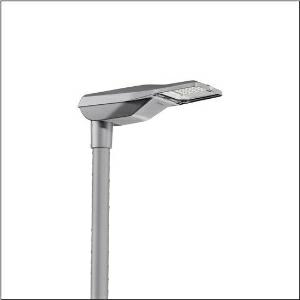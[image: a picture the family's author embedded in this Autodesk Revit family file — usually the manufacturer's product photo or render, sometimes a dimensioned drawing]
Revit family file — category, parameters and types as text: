
# Revit family: streetlight_sl_21_iq_micro___p0_5a_5xe1v31d08db_e47d
name_source: partatom
category: Lighting Fixtures
units: mm (PartAtom-declared; Revit-internal decimal feet)

## family parameters
Cut with Voids When Loaded = No
Host = Face
Light Source = No
Part Type = Normal
Room Calculation Point = No
Round Connector Dimension = Use Diameter
Shared = No

## types (1)
- --- (1 x LED, 4660 lm, 36.4 W, 3000K)
    Apparent Load = 36 VA
    CIE Flux Codes = 37 73 96 100 100
    Color Rendering = 70
    Color Temperature = 3000K
    Default Elevation = 1800 mm
    Description = Streetlight SL 21 iQ micro, mast luminaire, primary light control with lens, of PMMA, primary optical cover: cover, of toughened safety glass, transparent, light distribution: P0.5a, light emission: direct distribution, primary light characteristic: asymmetric, installation type: post-top, side-entry, LED, High Power LED, rated luminous flux: 4.660lm, luminous efficacy: 128lm/W, light colour: 730, colour temperature: 3000K, control gear: iQ-Comfort, control: pre-setting: linear dimming characteristic, Auto-Match, Temp-Guard, Lumen-Switch, Night-Set, Smart-Wire, Light-Fading, Desk-Remote (wireless, voltage-free reading and setting of iQ features in the workshop via application-optimized NFC function/RFID function), optimised constant luminous flux control (CLO 2.0), mains connection: 220..240V, AC, 50/60Hz, start of lifetime: 36W, end of service life: 38W, reduction: 16W, luminaire housing, of diecast aluminium, powder-coated, SITECO metallic grey (DB 702S), corrosivity category C5 high according to DIN EN ISO 12944, please order mast flange separately, inclination adjustable: 0°, 5°, 10°, 15°, sealing non-destructively replaceable, multi-level sealing system, length: 528mm, width: 235mm, height: 110mm, mast flange for spigot size: 42mm (side-entry): 5XC10008XM4, 60/48mm (side-entry/post-top): 5XC10108XM2, 76/60mm (side-entry/post-top): 5XC10108XM1, protection rating (complete): IP66, insulation class (complete): insulation class II (safety insulation), certification: CE, ENEC, ENEC+, VDE, impact resistance: IK10, permissible operating ambient temperature for outdoor applications: -40..+50°C, standard-compliant lighting for roads and squares, packaging unit: 1 piece

Light Distribution: P0.5a
    Height = 110 mm
    Lamp = 1 x LED
    Lamp Light Flux = 4660 lm
    Lamp Power = 36.4 W
    Lamp count = 1
    Length = 528 mm
    Luminous efficacy = 128 lm/W
    Manufacturer = Siteco
    ModVariant = No
    Model = 5XE1V31D08DB
    Number of Poles = 1
    OnlyDefault = Yes
    Power Factor = 1
    Product Name = Streetlight SL 21 iQ micro | P0.5a
    Product group = mast luminaire | pylon top
    ProductGroupID = 6100
    Protection Class = Protection class II
    Protection Degree = IP 66
    RLX_Detail_Level = 1
    RLX_Emergency_Light_Flux = 0 lm
    RLX_Emergency_Type = 0
    RLX_Emergency_Type_DB = No
    RlxData = <blob elided: 99325 chars, md5=adc8d52f>
    Socket = socket
    Standby Power = 0 W
    System Light Flux = 4660 lm
    System Power = 36 W
    Type Comments = factory setting: luminous flux: 100 % | dim-lin: 254 | 715 mA
    Type Image = l_1006881.jpg
    URL = http://relux.com
    VarID = @adj_078145
    Voltage = 0 V
    Weight = 0.00 kg
    Width = 235 mm

## geometry (parser evidence)
native form markers: Blend x4, Sweep x10
no freeform markers — native parametric forms only
